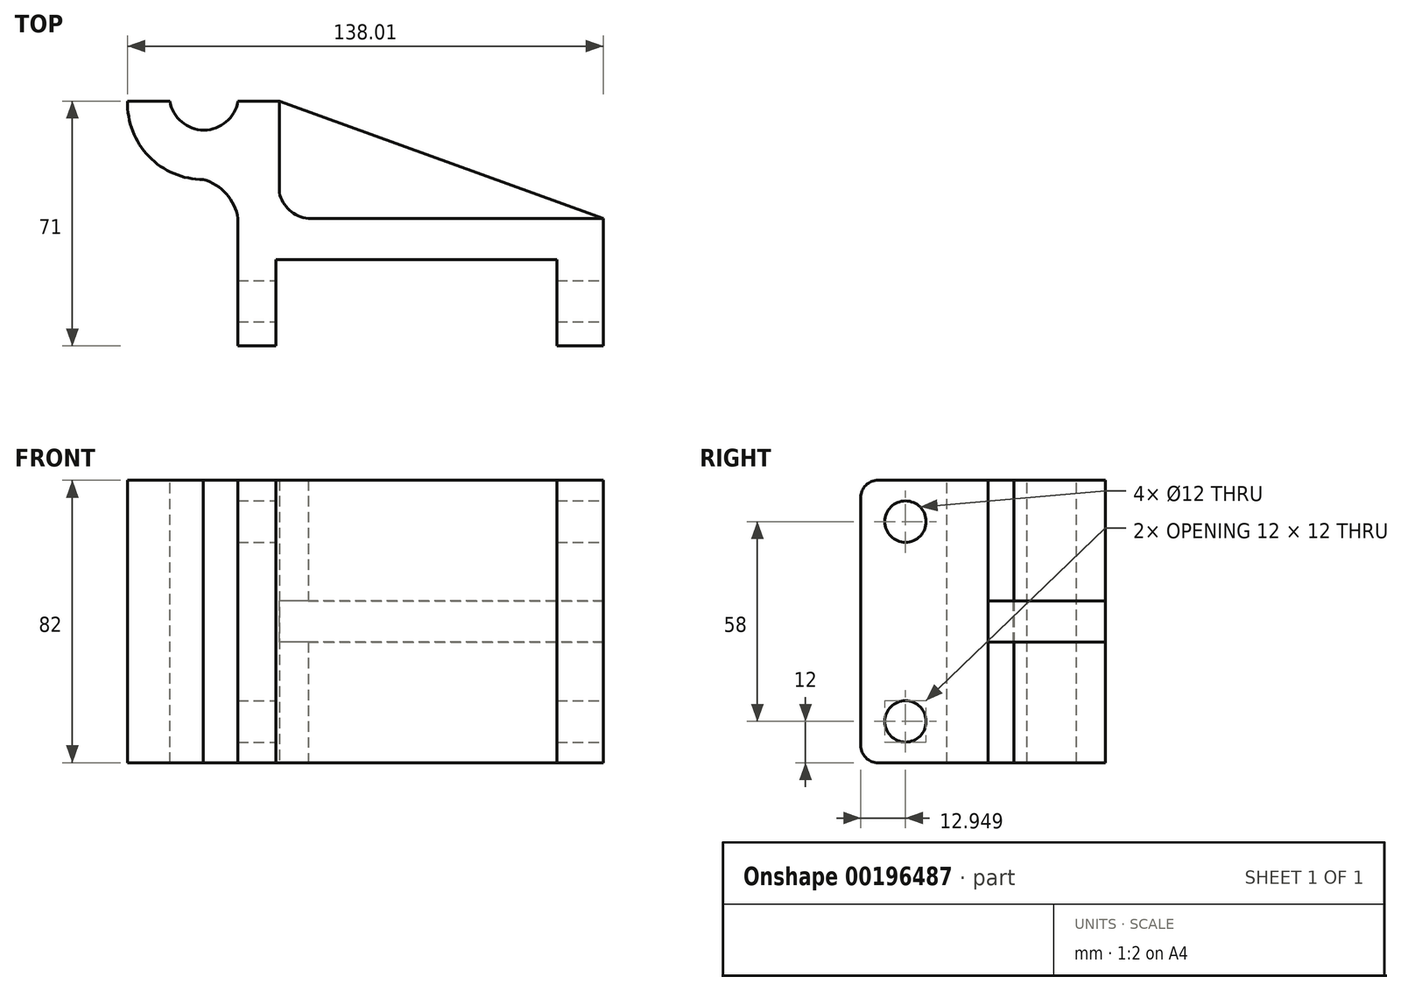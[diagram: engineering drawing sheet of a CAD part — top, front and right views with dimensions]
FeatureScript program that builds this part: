
annotation { "Feature Type Name" : "Feature", "Feature Type Description" : "" }
export const myFeature = defineFeature(function(context is Context, id is Id, definition is map)
    precondition{}
    {
        {
            var Q0;
            Q0=qCreatedBy(makeId("Front.planeOp"),FACE);
            var sketch = newSketch(context, id + "F0", { "sketchPlane" : qUnion([Q0])});
            skLineSegment(sketch, "E0.bottom", {"start": v(0, 0) * mm, "end": v(106, 0) * mm});
            skLineSegment(sketch, "E0.top", {"start": v(0, 82) * mm, "end": v(106, 82) * mm});
            skLineSegment(sketch, "E0.left", {"start": v(0, 0) * mm, "end": v(0, 82) * mm});
            skLineSegment(sketch, "E0.right", {"start": v(106, 0) * mm, "end": v(106, 82) * mm});
            skSolve(sketch);
        }
        {
            var Q0;
            Q0 = qSketchRegion(id + "F0", true);
            extrude(context, id + "F1", {"entities" : qUnion([Q0]), "depth" : 12 * mm});
        }
        {
            var Q0;
            Q0=makeQuery(id+"F1.opExtrude","CAP_FACE",FACE,{"disambiguationData":[OSD([sQuery(id+"F0.wireOp",EDGE,"E0.bottom"),sQuery(id+"F0.wireOp",EDGE,"E0.top"),sQuery(id+"F0.wireOp",EDGE,"E0.left"),sQuery(id+"F0.wireOp",EDGE,"E0.right")])],"isStart":false});
            var sketch = newSketch(context, id + "F2", { "sketchPlane" : qUnion([Q0])});
            skLineSegment(sketch, "E1.bottom", {"start": v(0, 82) * mm, "end": v(10.96, 82) * mm});
            skLineSegment(sketch, "E1.top", {"start": v(0, 0) * mm, "end": v(10.96, 0) * mm});
            skLineSegment(sketch, "E1.left", {"start": v(0, 82) * mm, "end": v(0, 0) * mm});
            skLineSegment(sketch, "E1.right", {"start": v(10.96, 82) * mm, "end": v(10.96, 0) * mm});
            skLineSegment(sketch, "E2.bottom", {"start": v(106, 0) * mm, "end": v(92.55, 0) * mm});
            skLineSegment(sketch, "E2.top", {"start": v(106, 82) * mm, "end": v(92.55, 82) * mm});
            skLineSegment(sketch, "E2.left", {"start": v(106, 0) * mm, "end": v(106, 82) * mm});
            skLineSegment(sketch, "E2.right", {"start": v(92.55, 0) * mm, "end": v(92.55, 82) * mm});
            skSolve(sketch);
        }
        {
            var Q0;
            Q0 = qSketchRegion(id + "F2", true);
            extrude(context, id + "F3", {"entities" : qUnion([Q0]), "operationType" : NewBodyOperationType.ADD, "depth" : 25 * mm});
        }
        {
            var Q0;
            Q0=makeQuery(id+"F3.opExtrude","CAP_EDGE",EDGE,{"disambiguationData":[OSD([sQuery(id+"F2.wireOp",EDGE,"E2.bottom")])],"isStart":false});
            var Q1;
            Q1=makeQuery(id+"F3.opExtrude","CAP_EDGE",EDGE,{"disambiguationData":[OSD([sQuery(id+"F2.wireOp",EDGE,"E2.top")])],"isStart":false});
            var Q2;
            Q2=makeQuery(id+"F3.opExtrude","CAP_EDGE",EDGE,{"disambiguationData":[OSD([sQuery(id+"F2.wireOp",EDGE,"E1.bottom")])],"isStart":false});
            var Q3;
            Q3=makeQuery(id+"F3.opExtrude","CAP_EDGE",EDGE,{"disambiguationData":[OSD([sQuery(id+"F2.wireOp",EDGE,"E1.top")])],"isStart":false});
            fillet(context, id + "F4", {"entities" : qUnion([Q0, Q1, Q2, Q3]), "radius" : 5 * mm, "tangentPropagation" : true, "allowEdgeOverflow" : false});
        }
        {
            var Q0;
            Q0=makeQuery(id+"F3.boolean.opBoolean","MERGE",FACE,{"derivedFrom":[makeQuery(id+"F1.opExtrude","SWEPT_FACE",FACE,{"disambiguationData":[OSD([sQuery(id+"F0.wireOp",EDGE,"E0.bottom")])]}),makeQuery(id+"F3.opExtrude","SWEPT_FACE",FACE,{"disambiguationData":[OSD([sQuery(id+"F2.wireOp",EDGE,"E1.top")])]}),makeQuery(id+"F3.opExtrude","SWEPT_FACE",FACE,{"disambiguationData":[OSD([sQuery(id+"F2.wireOp",EDGE,"E2.bottom")])]})]});
            var Q1;
            Q1=makeQuery(id+"F3.boolean.opBoolean","MERGE",FACE,{"derivedFrom":[makeQuery(id+"F1.opExtrude","SWEPT_FACE",FACE,{"disambiguationData":[OSD([sQuery(id+"F0.wireOp",EDGE,"E0.top")])]}),makeQuery(id+"F3.opExtrude","SWEPT_FACE",FACE,{"disambiguationData":[OSD([sQuery(id+"F2.wireOp",EDGE,"E1.bottom")])]}),makeQuery(id+"F3.opExtrude","SWEPT_FACE",FACE,{"disambiguationData":[OSD([sQuery(id+"F2.wireOp",EDGE,"E2.top")])]})]});
            cPlane(context, id + "F5", {"entities" : qUnion([Q0, Q1]), "cplaneType" : CPlaneType.MID_PLANE, "offset" : 25 * mm, "width" : 150 * mm, "height" : 150 * mm});
        }
        {
            var Q0;
            Q0=qCreatedBy(id+"F5.planeOp",FACE);
            var sketch = newSketch(context, id + "F6", { "sketchPlane" : qUnion([Q0])});
            skLineSegment(sketch, "E3", {"start": v(106, 0) * mm, "end": v(12.07, -34) * mm});
            skLineSegment(sketch, "E4", {"start": v(12.07, -34) * mm, "end": v(12.07, 0) * mm});
            skLineSegment(sketch, "E5", {"start": v(12.07, 0) * mm, "end": v(106, 0) * mm});
            skSolve(sketch);
        }
        {
            var Q0;
            Q0 = qSketchRegion(id + "F6", true);
            extrude(context, id + "F7", {"entities" : qUnion([Q0]), "depth" : 6 * mm, "hasSecondDirection" : true, "secondDirectionOppositeDirection" : true, "secondDirectionDepth" : 6 * mm});
        }
        {
            var Q0;
            Q0=makeQuery(id+"F3.boolean.opBoolean","MERGE",FACE,{"derivedFrom":[makeQuery(id+"F1.opExtrude","SWEPT_FACE",FACE,{"disambiguationData":[OSD([sQuery(id+"F0.wireOp",EDGE,"E0.right")])]}),makeQuery(id+"F3.opExtrude","SWEPT_FACE",FACE,{"disambiguationData":[OSD([sQuery(id+"F2.wireOp",EDGE,"E2.left")])]})]});
            var sketch = newSketch(context, id + "F8", { "sketchPlane" : qUnion([Q0])});
            skCircle(sketch, "E6", {"center": v(-24.05, 12) * mm, "radius": 6 * mm});
            skCircle(sketch, "E7", {"center": v(-24.05, 70) * mm, "radius": 6 * mm});
            skSolve(sketch);
        }
        {
            var Q0;
            Q0 = qSketchRegion(id + "F8", true);
            extrude(context, id + "F9", {"entities" : qUnion([Q0]), "operationType" : NewBodyOperationType.REMOVE, "oppositeDirection" : true, "depth" : 130 * mm});
        }
        {
            var Q0;
            Q0=qCreatedBy(makeId("Top.planeOp"),FACE);
            var sketch = newSketch(context, id + "F10", { "sketchPlane" : qUnion([Q0])});
            skLineSegment(sketch, "E8", {"start": v(0, 0) * mm, "end": v(0, 34) * mm});
            skLineSegment(sketch, "E9", {"start": v(0, 34) * mm, "end": v(12, 34) * mm});
            skLineSegment(sketch, "E10", {"start": v(12, 0) * mm, "end": v(0, 0) * mm});
            skLineSegment(sketch, "E11", {"start": v(12, 0) * mm, "end": v(12, 34) * mm});
            skArc(sketch, "E12", {"start": v(12, 7.49) * mm, "mid": v(15.78, 1.76) * mm, "end": v(22.42, 0) * mm});
            skLineSegment(sketch, "E13", {"start": v(12, 0) * mm, "end": v(22.42, 0) * mm});
            skSolve(sketch);
        }
        {
            var Q0;
            Q0 = qSketchRegion(id + "F10", true);
            extrude(context, id + "F11", {"entities" : qUnion([Q0]), "operationType" : NewBodyOperationType.ADD, "depth" : 82 * mm});
        }
        {
            var Q0;
            Q0 = qSketchRegion(id + "F10", true);
            extrude(context, id + "F12", {"entities" : qUnion([Q0]), "operationType" : NewBodyOperationType.ADD, "depth" : 25 * mm});
        }
        {
            var Q0;
            Q0=qCreatedBy(id+"F5.planeOp",FACE);
            var sketch = newSketch(context, id + "F13", { "sketchPlane" : qUnion([Q0])});
            skArc(sketch, "E14", {"start": v(-10, -11.27) * mm, "mid": v(-3.35, -7.1) * mm, "end": v(0, 0) * mm});
            skArc(sketch, "E15", {"start": v(-10, -11.27) * mm, "mid": v(-25.82, -17.97) * mm, "end": v(-32, -34) * mm});
            skLineSegment(sketch, "E16", {"start": v(-32, -34) * mm, "end": v(-19.73, -34) * mm});
            skLineSegment(sketch, "E17", {"start": v(0, -34) * mm, "end": v(0, 0) * mm});
            skArc(sketch, "E18", {"start": v(0, -34) * mm, "mid": v(-9.87, -25.62) * mm, "end": v(-19.73, -34) * mm});
            skSolve(sketch);
        }
        {
            var Q0;
            Q0 = qSketchRegion(id + "F13", true);
            extrude(context, id + "F14", {"entities" : qUnion([Q0]), "operationType" : NewBodyOperationType.ADD, "depth" : 41 * mm, "hasSecondDirection" : true, "secondDirectionOppositeDirection" : true, "secondDirectionDepth" : 41 * mm});
        }
    });
